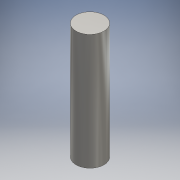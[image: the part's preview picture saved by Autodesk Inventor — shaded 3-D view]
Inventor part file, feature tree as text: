
AUTODESK INVENTOR PART (.ipt)
format: ipt  version: 2020.2 (Build 242310000, 310)  size: 89,600 bytes
history: native  units: mm
features: other x1, extrude x1, sketch x1
ambient origin geometry x8: Origin, YZ Plane, XZ Plane, XY Plane, X Axis, Y Axis, Z Axis, Center Point
bodies: Body1 (feature_tree)
feature tree (3):
  other  "ソリッド1"
  extrude  "押し出し1"  Depth=6.0mm
  sketch  "スケッチ1"
